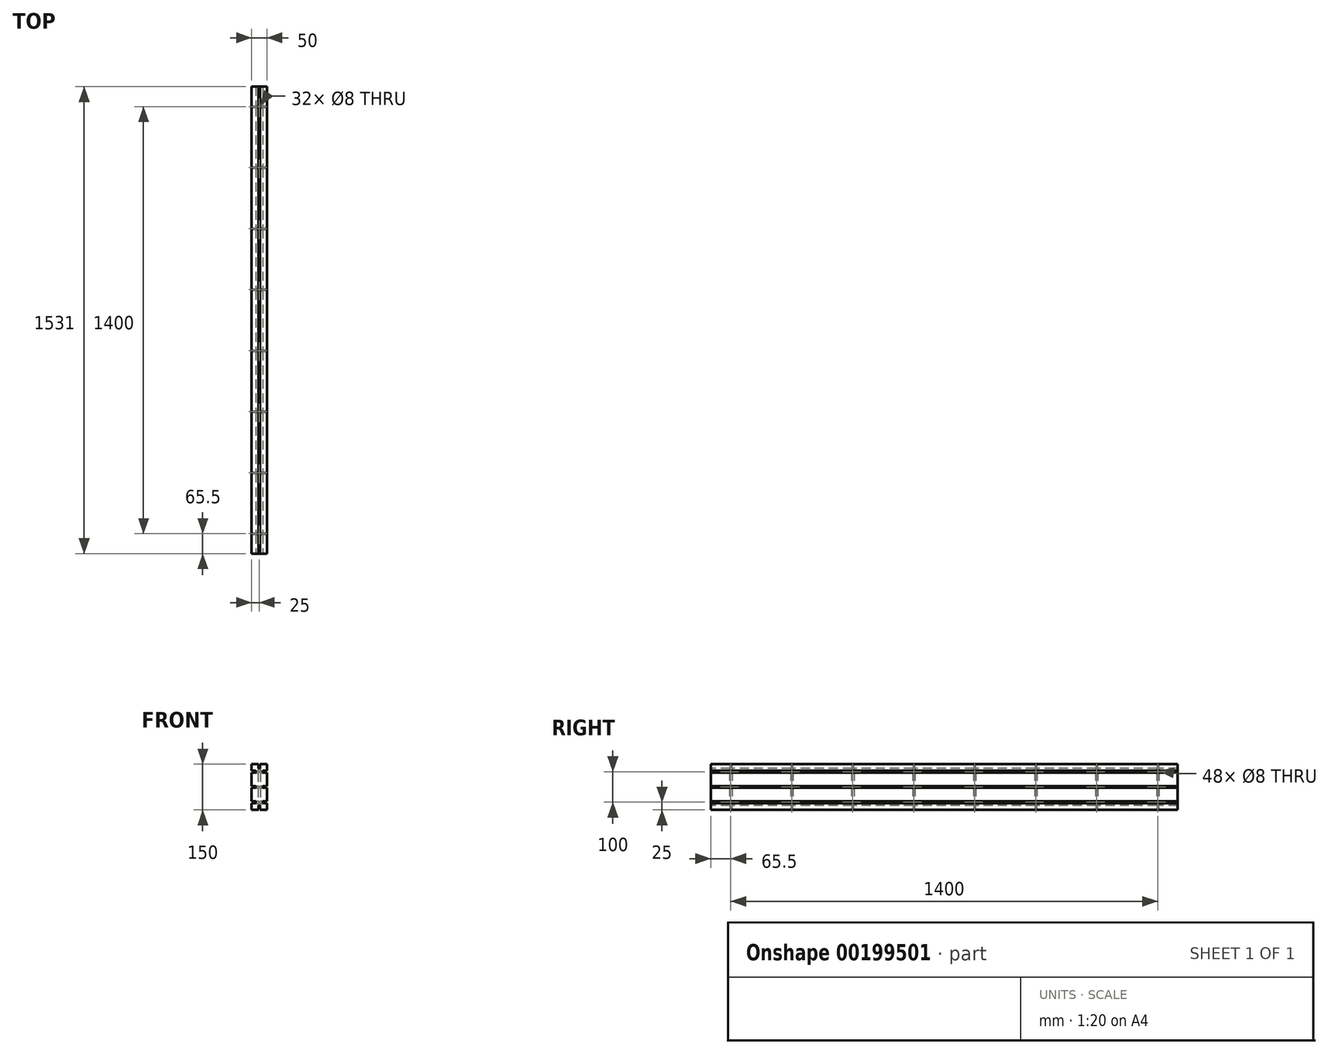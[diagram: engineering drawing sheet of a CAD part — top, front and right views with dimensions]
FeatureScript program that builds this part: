
annotation { "Feature Type Name" : "Feature", "Feature Type Description" : "" }
export const myFeature = defineFeature(function(context is Context, id is Id, definition is map)
    precondition{}
    {
        {
            var Q0;
            Q0=qCreatedBy(makeId("Front.planeOp"),FACE);
            var sketch = newSketch(context, id + "F0", { "sketchPlane" : qUnion([Q0])});
            skLineSegment(sketch, "E0.bottom", {"start": v(25, -75) * mm, "end": v(-25, -75) * mm});
            skLineSegment(sketch, "E0.top", {"start": v(25, 75) * mm, "end": v(-25, 75) * mm});
            skLineSegment(sketch, "E0.left", {"start": v(25, -75) * mm, "end": v(25, 75) * mm});
            skLineSegment(sketch, "E0.right", {"start": v(-25, -75) * mm, "end": v(-25, 75) * mm});
            skPoint(sketch, "E0.middle", {"position": v(0, 0) * mm});
            skSolve(sketch);
        }
        {
            var Q0;
            Q0 = qSketchRegion(id + "F0", true);
            extrude(context, id + "F1", {"entities" : qUnion([Q0]), "depth" : 1531 * mm});
        }
        {
            var Q0;
            Q0=makeQuery(id+"F1.opExtrude","SWEPT_FACE",FACE,{"disambiguationData":[OSD([sQuery(id+"F0.wireOp",EDGE,"E0.left")])]});
            var sketch = newSketch(context, id + "F2", { "sketchPlane" : qUnion([Q0])});
            skLineSegment(sketch, "E1", {"start": v(-1531, 0) * mm, "end": v(-640.44, 0) * mm, "construction": true});
            skCircle(sketch, "E2", {"center": v(-1465.5, 50) * mm, "radius": 4 * mm});
            skCircle(sketch, "E3.1.0.0", {"center": v(-1265.5, 50) * mm, "radius": 4 * mm});
            skCircle(sketch, "E3.2.0.0", {"center": v(-1065.5, 50) * mm, "radius": 4 * mm});
            skCircle(sketch, "E3.3.0.0", {"center": v(-865.5, 50) * mm, "radius": 4 * mm});
            skCircle(sketch, "E3.4.0.0", {"center": v(-665.5, 50) * mm, "radius": 4 * mm});
            skLineSegment(sketch, "E3.direction1", {"start": v(-1465.5, 50) * mm, "end": v(-1265.5, 50) * mm, "construction": true});
            skCircle(sketch, "E4.0.5.0", {"center": v(-465.5, 50) * mm, "radius": 4 * mm});
            skCircle(sketch, "E4.0.6.0", {"center": v(-265.5, 50) * mm, "radius": 4 * mm});
            skCircle(sketch, "E4.0.7.0", {"center": v(-65.5, 50) * mm, "radius": 4 * mm});
            skCircle(sketch, "E5.MirrorC", {"center": v(-1265.5, -50) * mm, "radius": 4 * mm});
            skCircle(sketch, "E6.MirrorC", {"center": v(-1065.5, -50) * mm, "radius": 4 * mm});
            skCircle(sketch, "E7.MirrorC", {"center": v(-865.5, -50) * mm, "radius": 4 * mm});
            skCircle(sketch, "E8.MirrorC", {"center": v(-65.5, -50) * mm, "radius": 4 * mm});
            skCircle(sketch, "E9.MirrorC", {"center": v(-265.5, -50) * mm, "radius": 4 * mm});
            skCircle(sketch, "E10.MirrorC", {"center": v(-665.5, -50) * mm, "radius": 4 * mm});
            skCircle(sketch, "E11.MirrorC", {"center": v(-465.5, -50) * mm, "radius": 4 * mm});
            skCircle(sketch, "E12.MirrorC", {"center": v(-1465.5, -50) * mm, "radius": 4 * mm});
            skCircle(sketch, "E13", {"center": v(-1465.5, 0) * mm, "radius": 4 * mm});
            skCircle(sketch, "E14.1.0.0", {"center": v(-1265.5, 0) * mm, "radius": 4 * mm});
            skCircle(sketch, "E14.2.0.0", {"center": v(-1065.5, 0) * mm, "radius": 4 * mm});
            skLineSegment(sketch, "E14.direction1", {"start": v(-1465.5, 0) * mm, "end": v(-1265.5, 0) * mm, "construction": true});
            skCircle(sketch, "E15.0.3.0", {"center": v(-865.5, 0) * mm, "radius": 4 * mm});
            skCircle(sketch, "E15.0.4.0", {"center": v(-665.5, 0) * mm, "radius": 4 * mm});
            skCircle(sketch, "E15.0.5.0", {"center": v(-465.5, 0) * mm, "radius": 4 * mm});
            skCircle(sketch, "E15.0.6.0", {"center": v(-265.5, 0) * mm, "radius": 4 * mm});
            skCircle(sketch, "E15.0.7.0", {"center": v(-65.5, 0) * mm, "radius": 4 * mm});
            skLineSegment(sketch, "E16", {"start": v(-865.5, 50) * mm, "end": v(-665.5, 50) * mm, "construction": true});
            skLineSegment(sketch, "E17", {"start": v(-765.5, 50) * mm, "end": v(-765.5, -75) * mm, "construction": true});
            skLineSegment(sketch, "E18", {"start": v(-1465.5, 50) * mm, "end": v(-1465.5, 0) * mm, "construction": true});
            skSolve(sketch);
        }
        {
            var Q0;
            Q0 = qSketchRegion(id + "F2", true);
            extrude(context, id + "F3", {"entities" : qUnion([Q0]), "operationType" : NewBodyOperationType.REMOVE, "endBound" : BoundingType.THROUGH_ALL, "oppositeDirection" : true, "depth" : 25 * mm});
        }
        {
            var Q0;
            Q0=makeQuery(id+"F1.opExtrude","SWEPT_FACE",FACE,{"disambiguationData":[OSD([sQuery(id+"F0.wireOp",EDGE,"E0.bottom")])]});
            var sketch = newSketch(context, id + "F4", { "sketchPlane" : qUnion([Q0])});
            skLineSegment(sketch, "E19", {"start": v(0, 1531) * mm, "end": v(0, 1392.8) * mm, "construction": true});
            skCircle(sketch, "E20", {"center": v(0, 1465.5) * mm, "radius": 4 * mm});
            skCircle(sketch, "E21.0.1.0", {"center": v(0, 1265.5) * mm, "radius": 4 * mm});
            skCircle(sketch, "E21.0.2.0", {"center": v(0, 1065.5) * mm, "radius": 4 * mm});
            skCircle(sketch, "E21.0.3.0", {"center": v(0, 865.5) * mm, "radius": 4 * mm});
            skCircle(sketch, "E21.0.4.0", {"center": v(0, 665.5) * mm, "radius": 4 * mm});
            skCircle(sketch, "E21.0.5.0", {"center": v(0, 465.5) * mm, "radius": 4 * mm});
            skCircle(sketch, "E21.0.6.0", {"center": v(0, 265.5) * mm, "radius": 4 * mm});
            skCircle(sketch, "E21.0.7.0", {"center": v(0, 65.5) * mm, "radius": 4 * mm});
            skLineSegment(sketch, "E21.direction1", {"start": v(0, 1465.5) * mm, "end": v(25, 1465.5) * mm, "construction": true});
            skLineSegment(sketch, "E21.direction2", {"start": v(0, 1465.5) * mm, "end": v(0, 1265.5) * mm, "construction": true});
            skLineSegment(sketch, "E22", {"start": v(0, 865.5) * mm, "end": v(0, 665.5) * mm, "construction": true});
            skLineSegment(sketch, "E23", {"start": v(0, 765.5) * mm, "end": v(25, 765.5) * mm, "construction": true});
            skPoint(sketch, "E23.endSnap0", {"position": v(0, 765.5) * mm});
            skSolve(sketch);
        }
        {
            var Q0;
            Q0 = qSketchRegion(id + "F4", true);
            extrude(context, id + "F5", {"entities" : qUnion([Q0]), "operationType" : NewBodyOperationType.REMOVE, "endBound" : BoundingType.THROUGH_ALL, "oppositeDirection" : true, "depth" : 25 * mm});
        }
        {
            var Q0;
            Q0=makeQuery(id+"F1.opExtrude","CAP_FACE",FACE,{"disambiguationData":[OSD([sQuery(id+"F0.wireOp",EDGE,"E0.bottom"),sQuery(id+"F0.wireOp",EDGE,"E0.top"),sQuery(id+"F0.wireOp",EDGE,"E0.left"),sQuery(id+"F0.wireOp",EDGE,"E0.right")])],"isStart":false});
            var sketch = newSketch(context, id + "F6", { "sketchPlane" : qUnion([Q0])});
            skLineSegment(sketch, "E24", {"start": v(0, 75) * mm, "end": v(0, -75) * mm, "construction": true});
            skLineSegment(sketch, "E25", {"start": v(-25, 50) * mm, "end": v(25, 50) * mm, "construction": true});
            skLineSegment(sketch, "E26.bottom", {"start": v(3, 61) * mm, "end": v(-3, 61) * mm});
            skLineSegment(sketch, "E26.top", {"start": v(3, 75) * mm, "end": v(-3, 75) * mm});
            skLineSegment(sketch, "E26.left", {"start": v(3, 61) * mm, "end": v(3, 75) * mm});
            skLineSegment(sketch, "E26.right", {"start": v(-3, 61) * mm, "end": v(-3, 75) * mm});
            skPoint(sketch, "E26.middle", {"position": v(0, 68) * mm});
            skLineSegment(sketch, "E27", {"start": v(-25, 0) * mm, "end": v(25, 0) * mm, "construction": true});
            skLineSegment(sketch, "E28.MirrorCS", {"start": v(-3, -61) * mm, "end": v(-3, -75) * mm});
            skLineSegment(sketch, "E29.MirrorCS", {"start": v(3, -75) * mm, "end": v(-3, -75) * mm});
            skLineSegment(sketch, "E30.MirrorCS", {"start": v(3, -61) * mm, "end": v(3, -75) * mm});
            skLineSegment(sketch, "E31.MirrorCS", {"start": v(3, -61) * mm, "end": v(-3, -61) * mm});
            skLineSegment(sketch, "E32.bottom", {"start": v(-25, 47) * mm, "end": v(-11, 47) * mm});
            skLineSegment(sketch, "E32.top", {"start": v(-25, 53) * mm, "end": v(-11, 53) * mm});
            skLineSegment(sketch, "E32.left", {"start": v(-25, 47) * mm, "end": v(-25, 53) * mm});
            skLineSegment(sketch, "E32.right", {"start": v(-11, 47) * mm, "end": v(-11, 53) * mm});
            skPoint(sketch, "E32.middle", {"position": v(-18, 50) * mm});
            skLineSegment(sketch, "E33.bottom", {"start": v(-25, -3) * mm, "end": v(-11, -3) * mm});
            skLineSegment(sketch, "E33.top", {"start": v(-25, 3) * mm, "end": v(-11, 3) * mm});
            skLineSegment(sketch, "E33.left", {"start": v(-25, -3) * mm, "end": v(-25, 3) * mm});
            skLineSegment(sketch, "E33.right", {"start": v(-11, -3) * mm, "end": v(-11, 3) * mm});
            skPoint(sketch, "E33.middle", {"position": v(-18, 0) * mm});
            skLineSegment(sketch, "E34.MirrorCS", {"start": v(-25, -47) * mm, "end": v(-11, -47) * mm});
            skLineSegment(sketch, "E35.MirrorCS", {"start": v(-25, -53) * mm, "end": v(-11, -53) * mm});
            skLineSegment(sketch, "E36.MirrorCS", {"start": v(-11, -47) * mm, "end": v(-11, -53) * mm});
            skLineSegment(sketch, "E37.MirrorCS", {"start": v(-25, -47) * mm, "end": v(-25, -53) * mm});
            skLineSegment(sketch, "E38.MirrorCS", {"start": v(25, 47) * mm, "end": v(11, 47) * mm});
            skLineSegment(sketch, "E39.MirrorCS", {"start": v(25, 53) * mm, "end": v(11, 53) * mm});
            skLineSegment(sketch, "E40.MirrorCS", {"start": v(11, 47) * mm, "end": v(11, 53) * mm});
            skLineSegment(sketch, "E41.MirrorCS", {"start": v(25, 47) * mm, "end": v(25, 53) * mm});
            skLineSegment(sketch, "E42.MirrorCS", {"start": v(25, -3) * mm, "end": v(11, -3) * mm});
            skLineSegment(sketch, "E43.MirrorCS", {"start": v(25, 3) * mm, "end": v(11, 3) * mm});
            skLineSegment(sketch, "E44.MirrorCS", {"start": v(11, -3) * mm, "end": v(11, 3) * mm});
            skLineSegment(sketch, "E45.MirrorCS", {"start": v(25, -3) * mm, "end": v(25, 3) * mm});
            skLineSegment(sketch, "E46.MirrorCS", {"start": v(25, -47) * mm, "end": v(11, -47) * mm});
            skLineSegment(sketch, "E47.MirrorCS", {"start": v(25, -53) * mm, "end": v(11, -53) * mm});
            skLineSegment(sketch, "E48.MirrorCS", {"start": v(11, -47) * mm, "end": v(11, -53) * mm});
            skLineSegment(sketch, "E49.MirrorCS", {"start": v(25, -47) * mm, "end": v(25, -53) * mm});
            skSolve(sketch);
        }
        {
            var Q0;
            Q0 = qSketchRegion(id + "F6", true);
            extrude(context, id + "F7", {"entities" : qUnion([Q0]), "operationType" : NewBodyOperationType.REMOVE, "endBound" : BoundingType.THROUGH_ALL, "oppositeDirection" : true, "depth" : 25 * mm});
        }
    });
